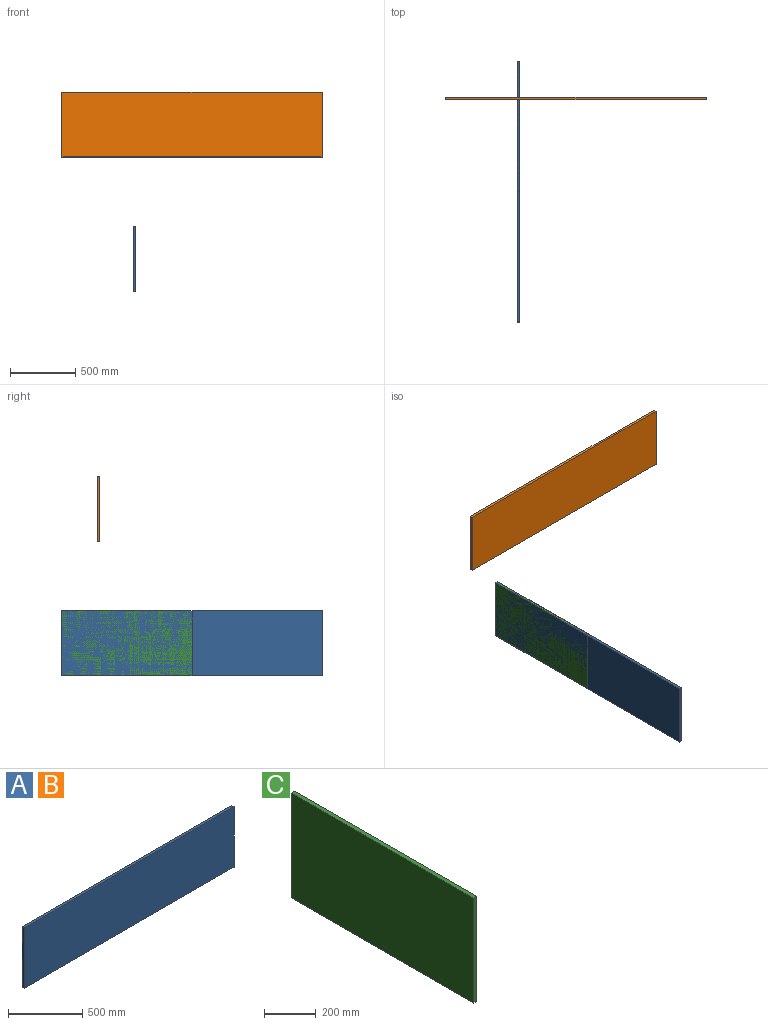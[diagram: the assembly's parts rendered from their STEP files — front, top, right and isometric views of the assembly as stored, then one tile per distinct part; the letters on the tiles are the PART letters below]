
ASSEMBLY  parts=3 mates=1
PART A: 10 faces, bbox 2000x20x500 mm
  f0: plane 2000x20mm, normal (0,0,-1), area 20200mm2, adj f1,f2,f3,f5,f6,f7,f8
  f1: plane 2000x500mm, normal (0,-1,0), area 996040mm2, adj f0,f2,f3,f4,f6,f8,f9
  f2: plane 500x20mm, normal (-1,0,0), area 10000mm2, adj f0,f1,f4,f5
  f3: plane 500x20mm, normal (1,0,0), area 10000mm2, adj f0,f1,f4,f5
  f4: plane 2000x20mm, normal (0,0,1), area 40000mm2, adj f1,f2,f3,f5
  f5: plane 2000x500mm, normal (0,1,0), area 1000000mm2, adj f0,f2,f3,f4
  f6: plane 10x2mm, normal (1,0,0), area 20mm2, adj f0,f1,f7,f9
  f7: plane 1980x2mm, normal (0,-1,0), area 3960mm2, adj f0,f6,f8,f9
  f8: plane 10x2mm, normal (-1,0,0), area 20mm2, adj f0,f1,f7,f9
  f9: plane 1980x10mm, normal (0,0,-1), area 19800mm2, adj f1,f6,f7,f8
PART B: same geometry as A
PART C: 8 faces, bbox 20x1000x500 mm
  f0: plane 500x20mm, normal (0,-1,0), area 9980mm2, adj f1,f2,f4,f5,f6,f7
  f1: plane 1000x10mm, normal (0,0,-1), area 10000mm2, adj f0,f3,f5,f6
  f2: plane 1000x498mm, normal (-1,0,0), area 498000mm2, adj f0,f3,f4,f7
  f3: plane 500x20mm, normal (0,1,0), area 9980mm2, adj f1,f2,f4,f5,f6,f7
  f4: plane 1000x20mm, normal (0,0,1), area 20000mm2, adj f0,f2,f3,f5
  f5: plane 1000x500mm, normal (1,0,0), area 500000mm2, adj f0,f1,f3,f4
  f6: plane 1000x2mm, normal (-1,0,0), area 2000mm2, adj f0,f1,f3,f7
  f7: plane 1000x10mm, normal (0,0,-1), area 10000mm2, adj f0,f2,f3,f6
PLACE A rot(axis=(0,0,1),90deg) t=(548.7,-1728.16,-1036.87)mm
PLACE B at identity
PLACE C t=(548.7,-728.16,-1036.87)mm
MATE fastened A.f1 <-> C.f5  axis (1,0,0) through (568.7,271.84,-786.87)mm
